# Revit family: Bath-Freestanding-Caroma Liano 1525
name_source: partatom
category: Plumbing Fixtures
revit_build: Autodesk Revit MEP 2014 (Build: 20140709_2115(x64)
units: mm (PartAtom-declared; Revit-internal decimal feet)

## types (1)
- Standard
    Assembly Code = D2010510
    CW Connection = No
    Default Elevation = 0 mm  [stored 0 ft]
    HW Connection = No
    Manufacturer = GWA Bathrooms & Kitchens
    Material_ANZRS = Porcelain-White-Caroma
    ModifiedIssue_ANZRS = 20151015.54 $
    Type Comments = Caroma Liano 1525 Freestanding Bath
    URL = http://www.specify.caroma.com.au
    Vent Connection = No
    WFU = 4
    Waste = Metal-Chrome-Caroma
    Waste Connection = Yes
    WasteDiameter = 60 mm  [stored 0.19685 ft]
    WasteOutlet_ANZRS = 0

note: [stored X ft] marks values corroborated as IEEE doubles in the binary element streams (Revit-internal decimal feet)

## geometry (parser evidence)
native form markers: Blend x10, Sweep x1
no freeform markers — native parametric forms only
